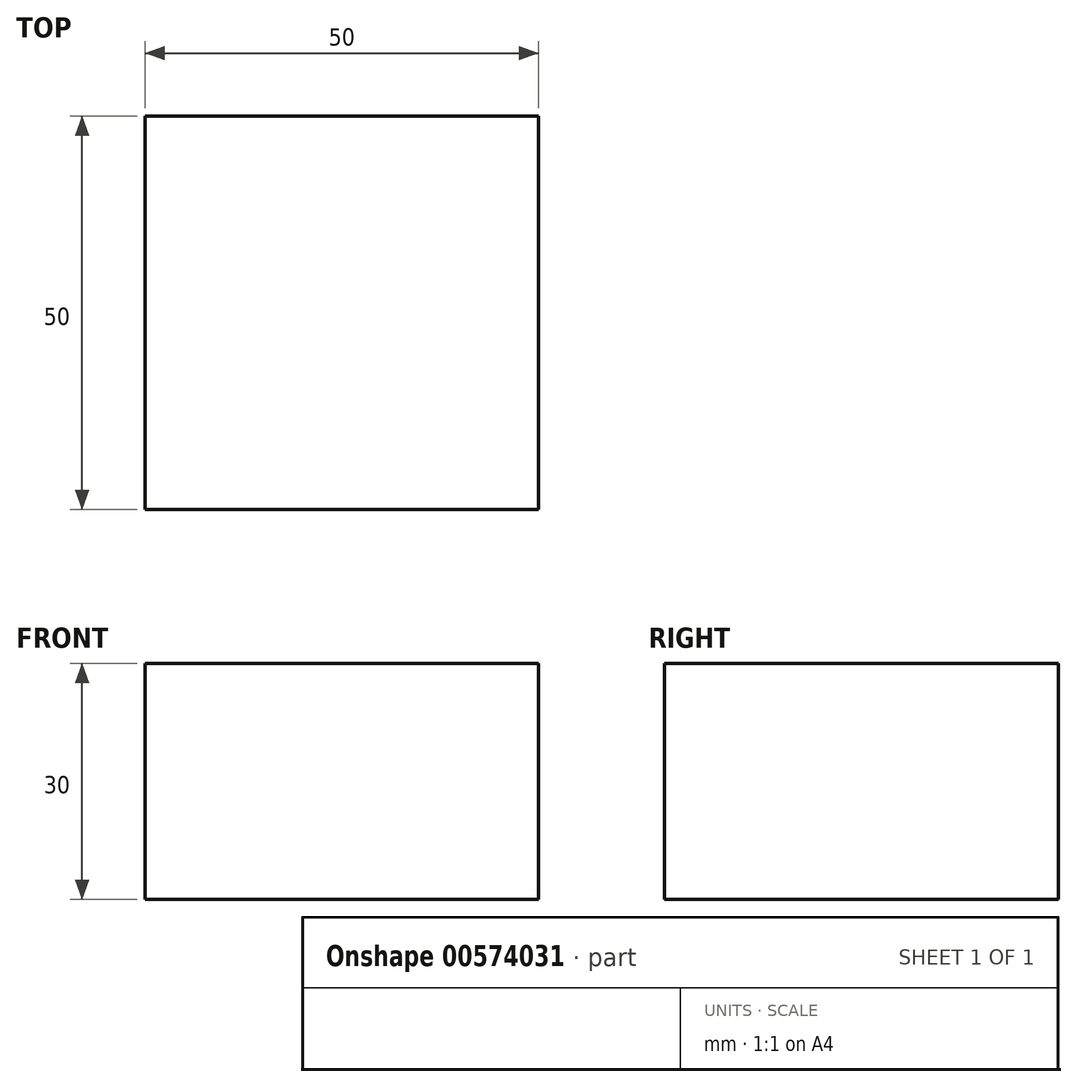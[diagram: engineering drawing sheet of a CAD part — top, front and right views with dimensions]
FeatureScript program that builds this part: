
annotation { "Feature Type Name" : "Feature", "Feature Type Description" : "" }
export const myFeature = defineFeature(function(context is Context, id is Id, definition is map)
    precondition{}
    {
        {
            var Q0;
            Q0=qCreatedBy(makeId("Top.planeOp"),FACE);
            var sketch = newSketch(context, id + "F0", { "sketchPlane" : qUnion([Q0])});
            skLineSegment(sketch, "E0.bottom", {"start": v(25, -25) * mm, "end": v(-25, -25) * mm});
            skLineSegment(sketch, "E0.top", {"start": v(25, 25) * mm, "end": v(-25, 25) * mm});
            skLineSegment(sketch, "E0.left", {"start": v(25, -25) * mm, "end": v(25, 25) * mm});
            skLineSegment(sketch, "E0.right", {"start": v(-25, -25) * mm, "end": v(-25, 25) * mm});
            skPoint(sketch, "E0.middle", {"position": v(0, 0) * mm});
            skSolve(sketch);
        }
        {
            var Q0;
            Q0=makeQuery(id+"F0.imprint","IMPRINT",FACE,{"disambiguationData":[TD([[makeQuery(id+"F0.imprint","IMPRINT",EDGE,{"derivedFrom":sQuery(id+"F0.wireOp",EDGE,"E0.bottom")}),-1.0]])]});
            extrude(context, id + "F1", {"entities" : qUnion([Q0]), "depth" : 30 * mm, "offsetDistance" : 25 * mm});
        }
    });
